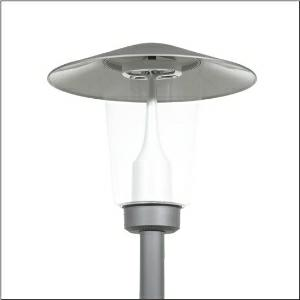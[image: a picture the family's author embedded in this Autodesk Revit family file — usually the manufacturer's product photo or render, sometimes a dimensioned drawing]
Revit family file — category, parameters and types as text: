
# Revit family: pilzleuchte_iq___p1_0a_5xa5235bf14hp_6096
name_source: partatom
category: Lighting Fixtures
units: mm (PartAtom-declared; Revit-internal decimal feet)

## family parameters
Cut with Voids When Loaded = No
Host = Face
Light Source = No
Part Type = Normal
Room Calculation Point = No
Round Connector Dimension = Use Diameter
Shared = No

## types (1)
- --- (1 x LED, 3920 lm, 33.6 W, 2200K)
    Apparent Load = 34 VA
    CIE Flux Codes = 35 64 90 96 100
    Color Rendering = 70
    Color Temperature = 2200K
    Default Elevation = 1800 mm
    Description = Mushroom Luminaire iQ, mast luminaire, Module 540 iQ-SR, primary light control with 3 zone facetted reflector, of plastic, silver coated, highly specular, structured, primary optical cover: cover, of PMMA, transparent, light distribution: P1.0a, light emission: direct distribution, primary light characteristic: strongly asymmetric, installation type: post-top, LED, High Power LED, rated luminous flux: 3.920lm, luminous efficacy: 117lm/W, light colour: 722, colour temperature: 2200K, control gear: iQ Street-Remote, control: pre-setting: logarithmic dimming characteristic, Street-Remote, Auto-Match, Temp-Guard, Lumen-Switch, Night-Set, Smart-Wire, Light-Fading, Desk-Remote (wireless, voltage-free reading and setting of iQ features in the workshop via application-optimized NFC function/RFID function), optimised constant luminous flux control (CLO 2.0), with terminal, 6-pole, max. 2.5mm², mains connection: 230..240V, AC, 50/60Hz, start of lifetime: 34W, end of service life: 36W, reduction: 15W, luminaire housing, upper part, of glass-fibre reinforced polyester, coated, Siteco® metallic grey (DB 702S), diameter: 650mm, height: 586mm, spigot size: d x l = 76 x 70mm (post-top) | with reducer (optional accessory) 60 x 70mm, mounting height: 3..5m, post-top mast mounting element, of diecast aluminium, coated, Siteco® metallic grey (DB 702S), Module 540 iQ-SR, traffic white (RAL 9016), equipment: Power, protection rating (complete): IP65, insulation class (complete): insulation class II (safety insulation), certification: CE, ENEC, VDE, packaging unit: 1 piece

Light Distribution: P1.0a
    Height = 586 mm
    Lamp = 1 x LED
    Lamp Light Flux = 3920 lm
    Lamp Power = 33.6 W
    Lamp count = 1
    Length = 650 mm
    Luminous efficacy = 117 lm/W
    Manufacturer = Siteco
    ModVariant = No
    Model = 5XA5235BF14HP
    Number of Poles = 1
    OnlyDefault = Yes
    Power Factor = 1
    Product Name = Pilzleuchte iQ | P1.0a
    Product group = mast luminaire | pylon top
    ProductGroupID = 6100
    Protection Class = Protection class II
    Protection Degree = IP 65
    RLX_Detail_Level = 1
    RLX_Emergency_Light_Flux = 0 lm
    RLX_Emergency_Type = 0
    RLX_Emergency_Type_DB = No
    RlxData = <blob elided: 52065 chars, md5=4a0a75a2>
    Socket = socket
    Standby Power = 0 W
    System Light Flux = 3920 lm
    System Power = 34 W
    Type Comments = factory setting: luminous flux: 100 % | dim-lin: 254 | 695 mA
    Type Image = l_1006077.jpg
    URL = http://relux.com
    VarID = @adj_189918
    Voltage = 0 V
    Weight = 0.00 kg
    Width = 0 mm  [stored 0 ft]

note: [stored X ft] marks values corroborated as IEEE doubles in the binary element streams (Revit-internal decimal feet)

## geometry (parser evidence)
native form markers: Blend x4, Sweep x13
no freeform markers — native parametric forms only
